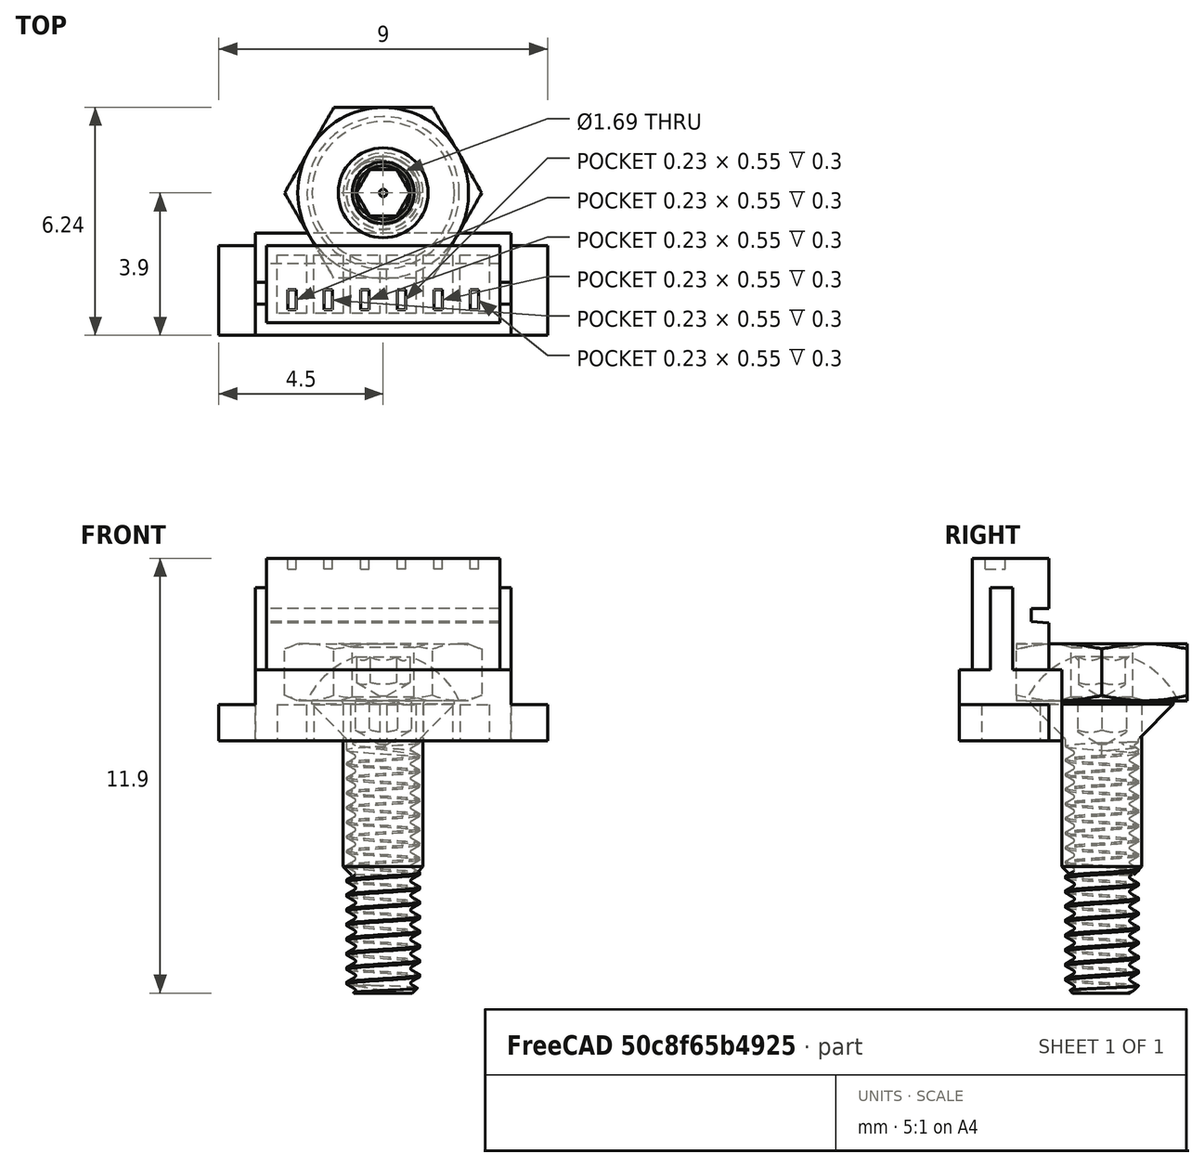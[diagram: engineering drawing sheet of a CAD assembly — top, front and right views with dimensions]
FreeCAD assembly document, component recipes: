
FREECAD ASSEMBLY — COMPONENT RECIPES ("PCBot")

This assembly document has 4 components, labeled P0..P3 below (a component is one placed body or linked part). 0 of them carry a construction recipe — the FreeCAD feature program that regenerates the part from scratch, quoted from this document or its linked companion documents; the rest are supplied as boundary geometry only. No exploded tour is included for this assembly.
COMPONENT P0 — geometry summary ("#2_nut"; no construction recipe available for this part):
  bounding box: 5.4 x 4.7 x 1.6 mm
  tessellated surface: 284 triangles
  volume: 26 mm^3 (65% of its bounding box)
  symmetry: 2-fold rotationally symmetric about the x axis; 2-fold rotationally symmetric about the z axis; mirror-symmetric across its y mid-plane, z mid-plane
COMPONENT P1 — geometry summary ("#2_screw"; no construction recipe available for this part):
  bounding box: 6.0 x 4.2 x 4.2 mm
  tessellated surface: 160 triangles
  volume: 27 mm^3 (26% of its bounding box)
  symmetry: mirror-symmetric across its y mid-plane
COMPONENT P2 — geometry summary ("m2_screw"; no construction recipe available for this part):
  bounding box: 8.0 x 3.9 x 3.9 mm
  tessellated surface: 344 triangles
  volume: 23 mm^3 (19% of its bounding box)
COMPONENT P3 — geometry summary ("SHR-06V-S-B001"; no construction recipe available for this part):
  bounding box: 9.0 x 5.0 x 2.8 mm
  tessellated surface: 292 triangles
  volume: 76 mm^3 (60% of its bounding box)
  symmetry: mirror-symmetric across its x mid-plane
PROVENANCE & LICENSES
A FreeCAD (.FCStd) document from a public repository crawl; recipes are the document's own serialized feature recipes (and, for linked parts, companion documents' recipes).
License: as declared in the source repository (recorded in the dataset sidecar).
